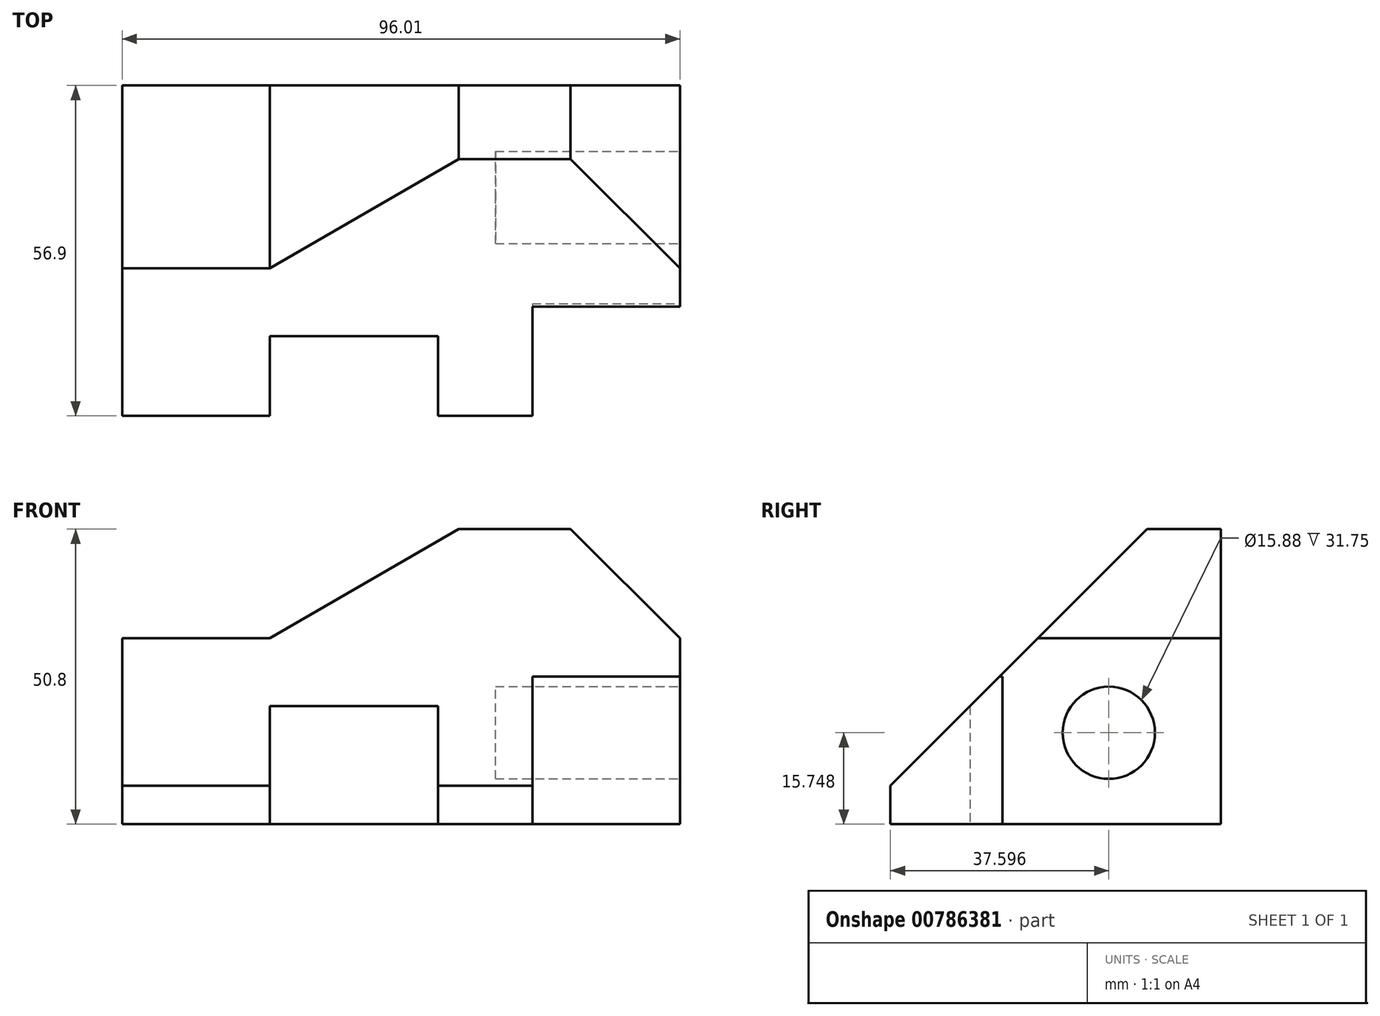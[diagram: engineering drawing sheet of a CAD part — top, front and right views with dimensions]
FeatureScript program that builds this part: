
annotation { "Feature Type Name" : "Feature", "Feature Type Description" : "" }
export const myFeature = defineFeature(function(context is Context, id is Id, definition is map)
    precondition{}
    {
        {
            var Q0;
            Q0=qCreatedBy(makeId("Front.planeOp"),FACE);
            var sketch = newSketch(context, id + "F0", { "sketchPlane" : qUnion([Q0])});
            skLineSegment(sketch, "E0.bottom", {"start": v(0, 0) * mm, "end": v(96.01, 0) * mm});
            skLineSegment(sketch, "E0.top", {"start": v(0, 50.8) * mm, "end": v(96.01, 50.8) * mm});
            skLineSegment(sketch, "E0.left", {"start": v(0, 0) * mm, "end": v(0, 50.8) * mm});
            skLineSegment(sketch, "E0.right", {"start": v(96.01, 0) * mm, "end": v(96.01, 50.8) * mm});
            skSolve(sketch);
        }
        {
            var Q0;
            Q0 = qSketchRegion(id + "F0", true);
            extrude(context, id + "F1", {"entities" : qUnion([Q0]), "depth" : 56.9 * mm, "offsetDistance" : 25.4 * mm});
        }
        {
            var Q0;
            Q0=makeQuery(id+"F1.opExtrude","SWEPT_FACE",FACE,{"disambiguationData":[OSD([sQuery(id+"F0.wireOp",EDGE,"E0.right")])]});
            var sketch = newSketch(context, id + "F2", { "sketchPlane" : qUnion([Q0])});
            skLineSegment(sketch, "E1", {"start": v(0, 50.8) * mm, "end": v(-12.7, 50.8) * mm});
            skLineSegment(sketch, "E2", {"start": v(-12.7, 50.8) * mm, "end": v(-56.9, 6.6) * mm});
            skLineSegment(sketch, "E3", {"start": v(-56.9, 6.6) * mm, "end": v(-56.9, 50.8) * mm});
            skLineSegment(sketch, "E4", {"start": v(-56.9, 50.8) * mm, "end": v(-12.7, 50.8) * mm});
            skSolve(sketch);
        }
        {
            var Q0;
            Q0 = qSketchRegion(id + "F2", true);
            extrude(context, id + "F3", {"entities" : qUnion([Q0]), "operationType" : NewBodyOperationType.REMOVE, "oppositeDirection" : true, "depth" : 96.01 * mm, "offsetDistance" : 25.4 * mm});
        }
        {
            var Q0;
            Q0=makeQuery(id+"F1.opExtrude","CAP_FACE",FACE,{"disambiguationData":[OSD([sQuery(id+"F0.wireOp",EDGE,"E0.bottom"),sQuery(id+"F0.wireOp",EDGE,"E0.top"),sQuery(id+"F0.wireOp",EDGE,"E0.left"),sQuery(id+"F0.wireOp",EDGE,"E0.right")])],"isStart":true});
            var sketch = newSketch(context, id + "F4", { "sketchPlane" : qUnion([Q0])});
            skLineSegment(sketch, "E5", {"start": v(0, 50.8) * mm, "end": v(0, 32) * mm});
            skLineSegment(sketch, "E6", {"start": v(0, 32) * mm, "end": v(-25.4, 32) * mm});
            skLineSegment(sketch, "E7", {"start": v(-25.4, 32) * mm, "end": v(-57.96, 50.8) * mm});
            skLineSegment(sketch, "E8", {"start": v(-57.96, 50.8) * mm, "end": v(0, 50.8) * mm});
            skSolve(sketch);
        }
        {
            var Q0;
            Q0 = qSketchRegion(id + "F4", true);
            extrude(context, id + "F5", {"entities" : qUnion([Q0]), "operationType" : NewBodyOperationType.REMOVE, "oppositeDirection" : true, "depth" : 56.9 * mm, "offsetDistance" : 25.4 * mm});
        }
        {
            var Q0;
            Q0=makeQuery(id+"F1.opExtrude","CAP_FACE",FACE,{"disambiguationData":[OSD([sQuery(id+"F0.wireOp",EDGE,"E0.bottom"),sQuery(id+"F0.wireOp",EDGE,"E0.top"),sQuery(id+"F0.wireOp",EDGE,"E0.left"),sQuery(id+"F0.wireOp",EDGE,"E0.right")])],"isStart":true});
            var sketch = newSketch(context, id + "F6", { "sketchPlane" : qUnion([Q0])});
            skLineSegment(sketch, "E9", {"start": v(-96.01, 50.8) * mm, "end": v(-77.22, 50.8) * mm});
            skLineSegment(sketch, "E10", {"start": v(-77.22, 50.8) * mm, "end": v(-96.01, 32) * mm});
            skLineSegment(sketch, "E11", {"start": v(-96.01, 32) * mm, "end": v(-96.01, 50.8) * mm});
            skSolve(sketch);
        }
        {
            var Q0;
            Q0 = qSketchRegion(id + "F6", true);
            extrude(context, id + "F7", {"entities" : qUnion([Q0]), "operationType" : NewBodyOperationType.REMOVE, "oppositeDirection" : true, "depth" : 56.9 * mm, "offsetDistance" : 25.4 * mm});
        }
        {
            var Q0;
            Q0=makeQuery(id+"F1.opExtrude","SWEPT_FACE",FACE,{"disambiguationData":[OSD([sQuery(id+"F0.wireOp",EDGE,"E0.right")])]});
            var sketch = newSketch(context, id + "F8", { "sketchPlane" : qUnion([Q0])});
            skLineSegment(sketch, "E12", {"start": v(0, 0) * mm, "end": v(-19.3, 0) * mm});
            skLineSegment(sketch, "E13", {"start": v(-19.3, 0) * mm, "end": v(-19.3, 15.75) * mm});
            skCircle(sketch, "E14", {"center": v(-19.3, 15.75) * mm, "radius": 7.94 * mm});
            skSolve(sketch);
        }
        {
            var Q0;
            Q0 = qSketchRegion(id + "F8", true);
            extrude(context, id + "F9", {"entities" : qUnion([Q0]), "operationType" : NewBodyOperationType.REMOVE, "oppositeDirection" : true, "depth" : 31.75 * mm, "offsetDistance" : 25.4 * mm});
        }
        {
            var Q0;
            Q0=makeQuery(id+"F1.opExtrude","CAP_FACE",FACE,{"disambiguationData":[OSD([sQuery(id+"F0.wireOp",EDGE,"E0.bottom"),sQuery(id+"F0.wireOp",EDGE,"E0.top"),sQuery(id+"F0.wireOp",EDGE,"E0.left"),sQuery(id+"F0.wireOp",EDGE,"E0.right")])],"isStart":false});
            var sketch = newSketch(context, id + "F10", { "sketchPlane" : qUnion([Q0])});
            skLineSegment(sketch, "E15", {"start": v(96.01, 0) * mm, "end": v(70.61, 0) * mm});
            skLineSegment(sketch, "E16", {"start": v(96.01, 0) * mm, "end": v(96.01, 25.4) * mm});
            skLineSegment(sketch, "E17", {"start": v(96.01, 25.4) * mm, "end": v(70.61, 25.4) * mm});
            skLineSegment(sketch, "E18", {"start": v(70.61, 25.4) * mm, "end": v(70.61, 0) * mm});
            skSolve(sketch);
        }
        {
            var Q0;
            Q0 = qSketchRegion(id + "F10", true);
            extrude(context, id + "F11", {"entities" : qUnion([Q0]), "operationType" : NewBodyOperationType.REMOVE, "oppositeDirection" : true, "depth" : 19.3 * mm, "offsetDistance" : 25.4 * mm});
        }
        {
            var Q0;
            Q0=makeQuery(id+"F1.opExtrude","CAP_FACE",FACE,{"disambiguationData":[OSD([sQuery(id+"F0.wireOp",EDGE,"E0.bottom"),sQuery(id+"F0.wireOp",EDGE,"E0.top"),sQuery(id+"F0.wireOp",EDGE,"E0.left"),sQuery(id+"F0.wireOp",EDGE,"E0.right")])],"isStart":false});
            var sketch = newSketch(context, id + "F12", { "sketchPlane" : qUnion([Q0])});
            skLineSegment(sketch, "E19", {"start": v(0, 0) * mm, "end": v(25.4, 0) * mm});
            skLineSegment(sketch, "E20", {"start": v(25.4, 0) * mm, "end": v(54.36, 0) * mm});
            skLineSegment(sketch, "E21", {"start": v(54.36, 0) * mm, "end": v(54.36, 20.32) * mm});
            skLineSegment(sketch, "E22", {"start": v(54.36, 20.32) * mm, "end": v(25.4, 20.32) * mm});
            skLineSegment(sketch, "E23", {"start": v(25.4, 20.32) * mm, "end": v(25.4, 0) * mm});
            skSolve(sketch);
        }
        {
            var Q0;
            Q0 = qSketchRegion(id + "F12", true);
            extrude(context, id + "F13", {"entities" : qUnion([Q0]), "operationType" : NewBodyOperationType.REMOVE, "oppositeDirection" : true, "depth" : 13.72 * mm, "offsetDistance" : 25.4 * mm});
        }
    });
